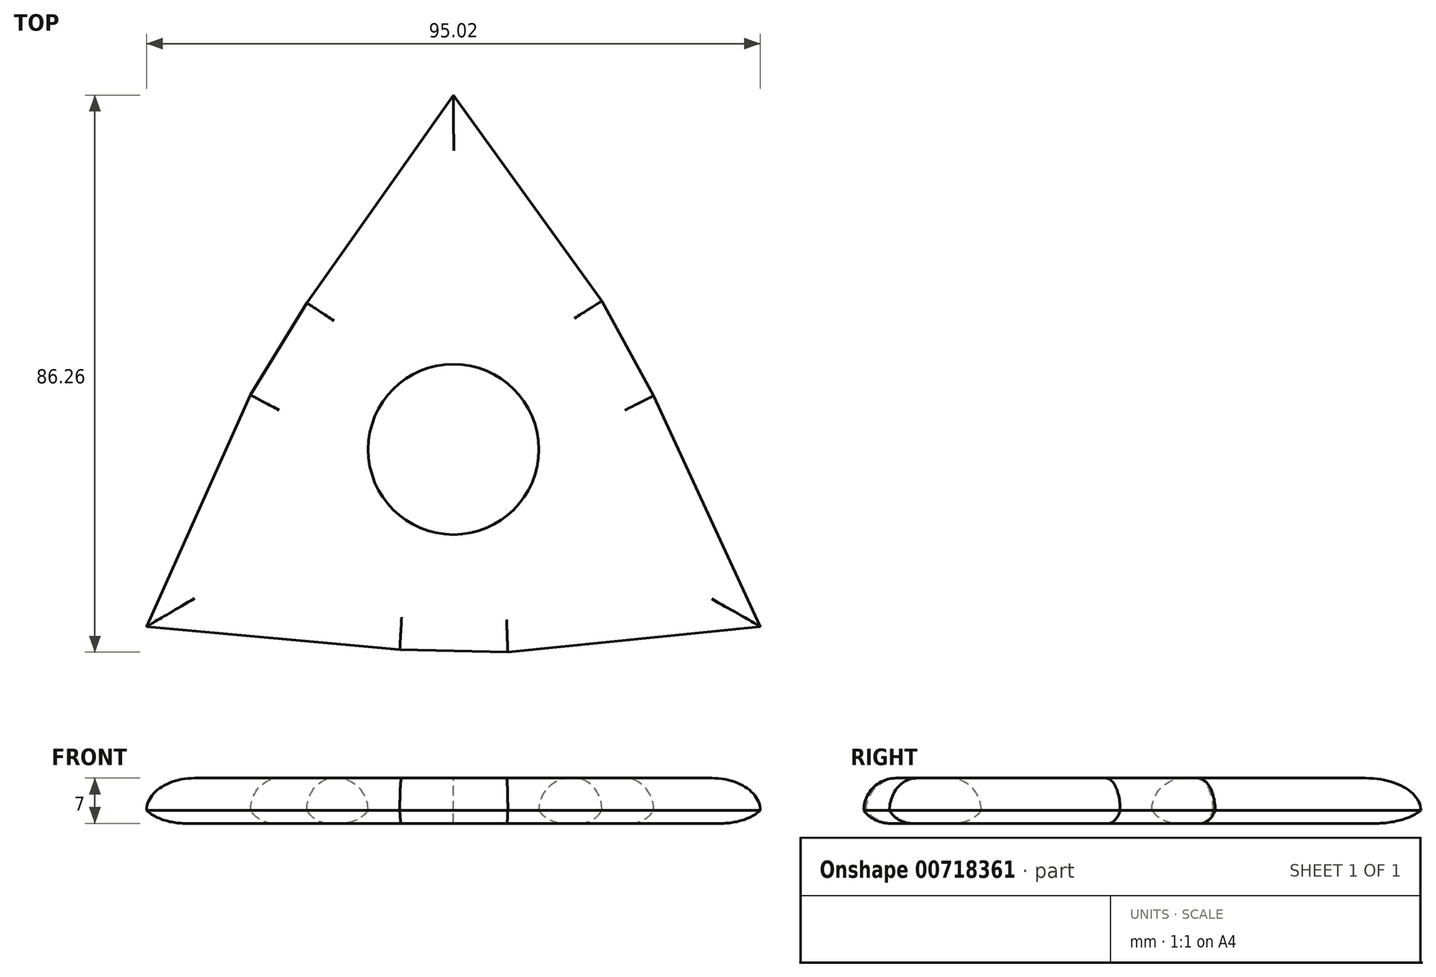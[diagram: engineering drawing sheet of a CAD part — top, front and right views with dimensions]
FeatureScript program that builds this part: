
annotation { "Feature Type Name" : "Feature", "Feature Type Description" : "" }
export const myFeature = defineFeature(function(context is Context, id is Id, definition is map)
    precondition{}
    {
        {
            var Q0;
            Q0=qCreatedBy(makeId("Top.planeOp"),FACE);
            var sketch = newSketch(context, id + "F0", { "sketchPlane" : qUnion([Q0])});
            skLineSegment(sketch, "E0", {"start": v(-22.7, 22.7) * mm, "end": v(0, 54.85) * mm});
            skLineSegment(sketch, "E1", {"start": v(0, 54.85) * mm, "end": v(23, 23) * mm});
            skLineSegment(sketch, "E2.1.0", {"start": v(-8.3, -31) * mm, "end": v(-47.5, -27.43) * mm});
            skLineSegment(sketch, "E2.1.1", {"start": v(-47.5, -27.43) * mm, "end": v(-31.41, 8.42) * mm});
            skLineSegment(sketch, "E2.2.0", {"start": v(31, 8.3) * mm, "end": v(47.5, -27.43) * mm});
            skLineSegment(sketch, "E2.2.1", {"start": v(47.5, -27.43) * mm, "end": v(8.42, -31.41) * mm});
            skPoint(sketch, "E2.center", {"position": v(0, 0) * mm});
            skLineSegment(sketch, "E3", {"start": v(-8.3, -31) * mm, "end": v(8.42, -31.41) * mm});
            skLineSegment(sketch, "E4", {"start": v(-22.7, 22.7) * mm, "end": v(-31.41, 8.42) * mm});
            skLineSegment(sketch, "E5", {"start": v(23, 23) * mm, "end": v(31, 8.3) * mm});
            skCircle(sketch, "E6", {"center": v(0, 0) * mm, "radius": 11.2 * mm});
            skCircle(sketch, "E7", {"center": v(0, 0) * mm, "radius": 13.2 * mm});
            skSolve(sketch);
        }
        {
            var Q0;
            Q0=makeQuery(id+"F0.imprint","IMPRINT",FACE,{"disambiguationData":[TD([[makeQuery(id+"F0.imprint","IMPRINT",EDGE,{"derivedFrom":sQuery(id+"F0.wireOp",EDGE,"E0")}),-1.0]])]});
            extrude(context, id + "F1", {"entities" : qUnion([Q0]), "depth" : 7 * mm, "offsetDistance" : 25 * mm});
        }
        {
            var Q0;
            Q0=makeQuery(id+"F1.opExtrude","CAP_FACE",FACE,{"disambiguationData":[OSD([sQuery(id+"F0.wireOp",EDGE,"E0"),sQuery(id+"F0.wireOp",EDGE,"E1"),sQuery(id+"F0.wireOp",EDGE,"E2.1.0"),sQuery(id+"F0.wireOp",EDGE,"E2.1.1"),sQuery(id+"F0.wireOp",EDGE,"E2.2.0"),sQuery(id+"F0.wireOp",EDGE,"E2.2.1"),sQuery(id+"F0.wireOp",EDGE,"E3"),sQuery(id+"F0.wireOp",EDGE,"E4"),sQuery(id+"F0.wireOp",EDGE,"E5"),sQuery(id+"F0.wireOp",EDGE,"E7")])],"isStart":false});
            fillet(context, id + "F2", {"entities" : qUnion([Q0]), "radius" : 5 * mm, "tangentPropagation" : true, "allowEdgeOverflow" : false});
        }
        {
            var Q0;
            Q0=makeQuery(id+"F1.opExtrude","CAP_FACE",FACE,{"disambiguationData":[OSD([sQuery(id+"F0.wireOp",EDGE,"E0"),sQuery(id+"F0.wireOp",EDGE,"E1"),sQuery(id+"F0.wireOp",EDGE,"E2.1.0"),sQuery(id+"F0.wireOp",EDGE,"E2.1.1"),sQuery(id+"F0.wireOp",EDGE,"E2.2.0"),sQuery(id+"F0.wireOp",EDGE,"E2.2.1"),sQuery(id+"F0.wireOp",EDGE,"E3"),sQuery(id+"F0.wireOp",EDGE,"E4"),sQuery(id+"F0.wireOp",EDGE,"E5"),sQuery(id+"F0.wireOp",EDGE,"E7")])],"isStart":true});
            fillet(context, id + "F3", {"entities" : qUnion([Q0]), "radius" : 5 * mm, "tangentPropagation" : true, "allowEdgeOverflow" : false});
        }
    });
